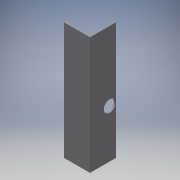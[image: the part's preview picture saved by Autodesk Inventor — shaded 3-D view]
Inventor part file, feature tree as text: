
AUTODESK INVENTOR PART (.ipt)
format: ipt  version: 2017 (Build 210142000, 142)  size: 102,400 bytes
history: native  units: in
note: dims shown in document units (in); Inventor stores cm internally (conversion verified against a paired STEP export)
features: other x3, extrude x2, sketch x2, reference x1
ambient origin geometry x8: Origin, YZ Plane, XZ Plane, XY Plane, X Axis, Y Axis, Z Axis, Center Point
bodies: Solid1 (feature_tree)
feature tree (8):
  extrude  "Extrusion1"  Depth=0.0625in
  extrude  "Extrusion2"  Depth=0.0625in
  sketch  "Sketch1"  dims[d0=1.0in d1=0.0625in]
  sketch  "Sketch2"  dims[d4=1.0in d5=0.0625in d6=4.5in d7=0.0in d8=1.8125in d9=0.0in]
  reference  "Reference1"
  other  "Robot Frame '16.iam"
  other  "Pickup 16:1"
  other  "Part8:1"
